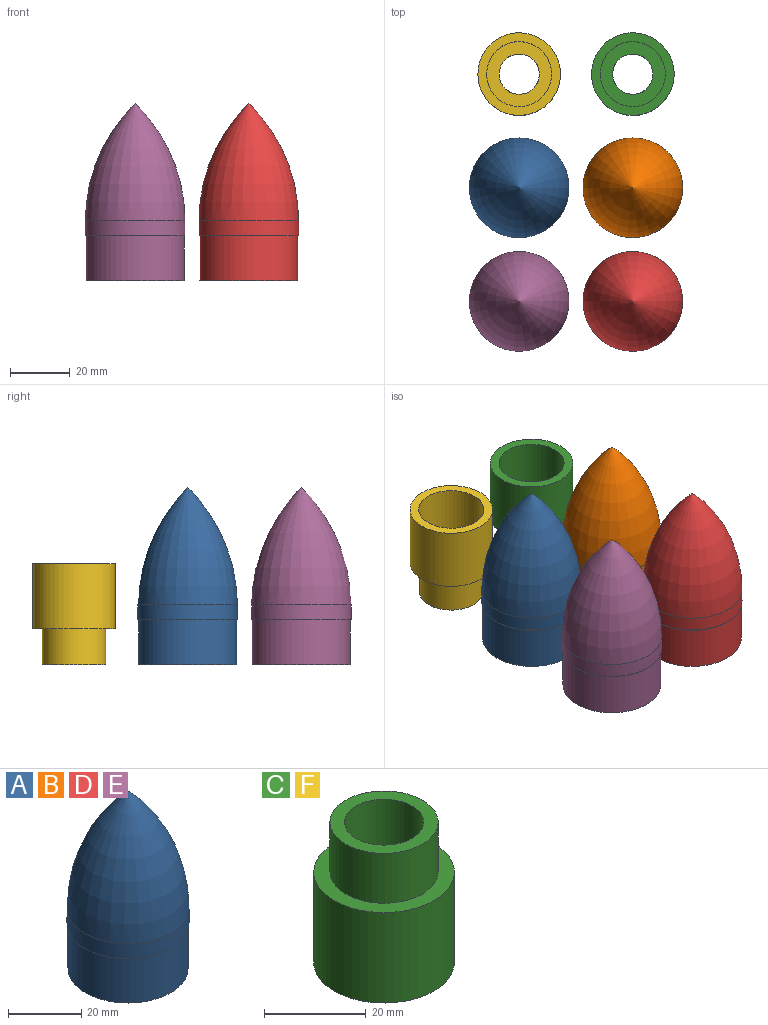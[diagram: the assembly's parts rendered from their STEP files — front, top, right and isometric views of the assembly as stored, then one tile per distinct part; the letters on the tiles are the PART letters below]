
ASSEMBLY  parts=6 mates=5
PART A: 7 faces, bbox 33.4x33.4x59.4 mm
  f0: cylinder r=16.44mm len=32.88mm, axis (0,0,-1), area 1549.2mm2, adj f1,f3
  f1: plane 32.88x32.88mm, normal (0,0,-1), area 156mm2, adj f0,f5
  f2: cylinder r=16.7mm len=33.4mm, axis (0,0,-1), area 524.6mm2, adj f3,f4
  f3: plane 33.4x33.4mm, normal (0,0,-1), area 27.3mm2, adj f0,f2
  f4: revolved ~39.38x33.4mm, area 3040mm2, adj f2
  f5: cylinder r=14.85mm len=29.7mm, axis (0,0,-1), area 2073.7mm2, adj f1,f6
  f6: plane 29.7x29.7mm, normal (0,0,-1), area 692.8mm2, adj f5
PART B: same geometry as A
PART C: 10 faces, bbox 27.7x27.7x33.8 mm
  f0: cylinder r=6.75mm len=13.5mm, axis (0,0,1), area 106mm2, adj f7,f8
  f1: cylinder r=13.85mm len=27.7mm, axis (0,0,-1), area 1897.1mm2, adj f2,f9
  f2: plane 27.7x27.7mm, normal (0,0,1), area 246.3mm2, adj f1,f5
  f3: cylinder r=10.9mm len=21.8mm, axis (0,0,-1), area 1260.2mm2, adj f8,f9
  f4: cylinder r=7.8mm len=15.6mm, axis (0,0,-1), area 632.2mm2, adj f6,f7
  f5: cylinder r=10.65mm len=21.3mm, axis (0,0,-1), area 803mm2, adj f2,f6
  f6: plane 21.3x21.3mm, normal (0,0,1), area 165.2mm2, adj f4,f5
  f7: plane 15.6x15.6mm, normal (0,0,1), area 48mm2, adj f0,f4
  f8: plane 21.8x21.8mm, normal (0,0,-1), area 230.1mm2, adj f0,f3
  f9: plane 27.7x27.7mm, normal (0,0,-1), area 229.4mm2, adj f1,f3
PART D: same geometry as A
PART E: same geometry as A
PART F: same geometry as C
PLACE A t=(42.47,17.52,30.05)mm
PLACE B t=(80.57,17.52,30.05)mm
PLACE C rot(axis=(0,1,0),180deg) t=(80.57,55.62,63.75)mm
PLACE D t=(80.57,-20.58,30.05)mm
PLACE E t=(42.47,-20.58,30.05)mm
PLACE F rot(axis=(0,1,0),180deg) t=(42.47,55.62,63.75)mm
MATE fastened D.f0 <-> B.f1  axis (0,0,-1) through (80.57,-20.58,30.05)mm
MATE fastened F.f4 <-> A.f1  axis (0,0,-1) through (42.47,55.62,30.05)mm
MATE fastened E.f2 <-> A.f1  axis (0,0,-1) through (42.47,-20.58,30.05)mm
MATE fastened B.f0 <-> A.f1  axis (0,0,-1) through (80.57,17.52,30.05)mm
MATE fastened C.f5 <-> B.f1  axis (0,0,-1) through (80.57,55.62,30.05)mm
